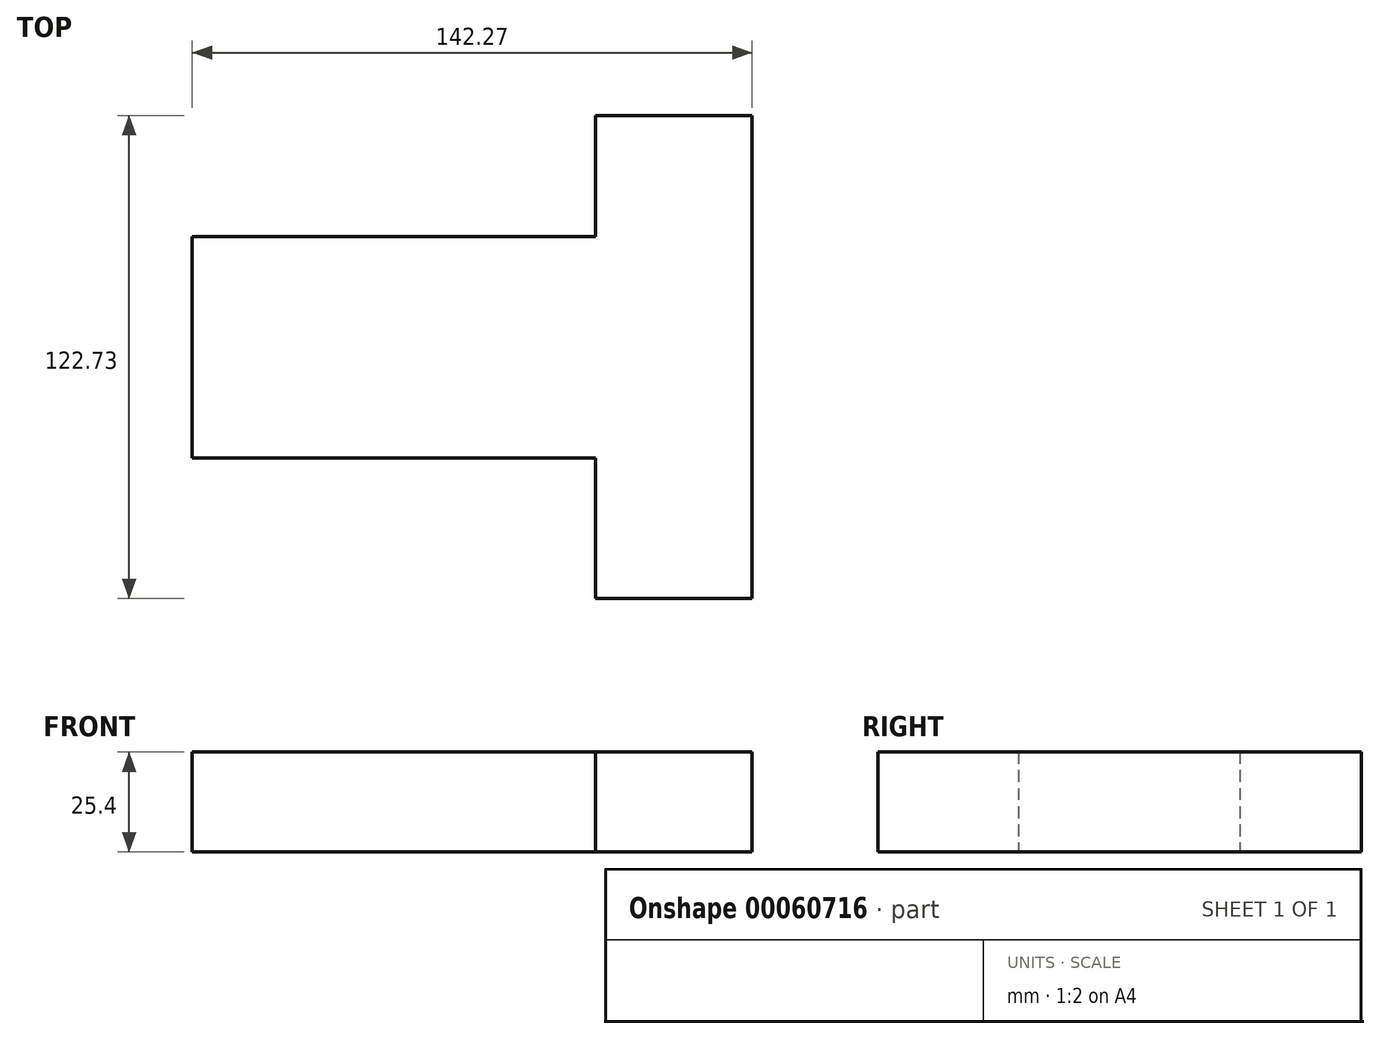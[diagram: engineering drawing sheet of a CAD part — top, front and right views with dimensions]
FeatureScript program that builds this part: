
annotation { "Feature Type Name" : "Feature", "Feature Type Description" : "" }
export const myFeature = defineFeature(function(context is Context, id is Id, definition is map)
    precondition{}
    {
        {
            var Q0;
            Q0=qCreatedBy(makeId("Top.planeOp"),FACE);
            var sketch = newSketch(context, id + "F0", { "sketchPlane" : qUnion([Q0])});
            skLineSegment(sketch, "E0.bottom", {"start": v(-116.4, 0) * mm, "end": v(-7.9, 0) * mm});
            skLineSegment(sketch, "E0.top", {"start": v(-116.4, 56.28) * mm, "end": v(-7.9, 56.28) * mm});
            skLineSegment(sketch, "E0.left", {"start": v(-116.4, 0) * mm, "end": v(-116.4, 56.28) * mm});
            skLineSegment(sketch, "E0.right", {"start": v(-7.9, 0) * mm, "end": v(-7.9, 56.28) * mm});
            skLineSegment(sketch, "E1.bottom", {"start": v(25.86, 87.07) * mm, "end": v(-13.98, 87.07) * mm});
            skLineSegment(sketch, "E1.top", {"start": v(25.86, -35.66) * mm, "end": v(-13.98, -35.66) * mm});
            skLineSegment(sketch, "E1.left", {"start": v(25.86, 87.07) * mm, "end": v(25.86, -35.66) * mm});
            skLineSegment(sketch, "E1.right", {"start": v(-13.98, 87.07) * mm, "end": v(-13.98, -35.66) * mm});
            skSolve(sketch);
        }
        {
            var Q0;
            {var subQ0=sQuery(id+"F0.wireOp",EDGE,"E0.left");Q0=makeQuery(id+"F0.imprint","IMPRINT",FACE,{"disambiguationData":[TD([[makeQuery(id+"F0.imprint","IMPRINT",EDGE,{"derivedFrom":subQ0}),-1.0]])]});}
            var Q1;
            {var subQ0=sQuery(id+"F0.wireOp",EDGE,"E0.right");Q1=makeQuery(id+"F0.imprint","IMPRINT",FACE,{"disambiguationData":[TD([[makeQuery(id+"F0.imprint","IMPRINT",EDGE,{"derivedFrom":subQ0}),1.0]])]});}
            var Q2;
            {var subQ1=sQuery(id+"F0.wireOp",EDGE,"E0.right");Q2=makeQuery(id+"F0.imprint","IMPRINT",FACE,{"disambiguationData":[TD([[makeQuery(id+"F0.imprint","IMPRINT",EDGE,{"derivedFrom":subQ1}),-1.0]])]});}
            extrude(context, id + "F1", {"entities" : qUnion([Q0, Q1, Q2]), "depth" : 25.4 * mm});
        }
    });
